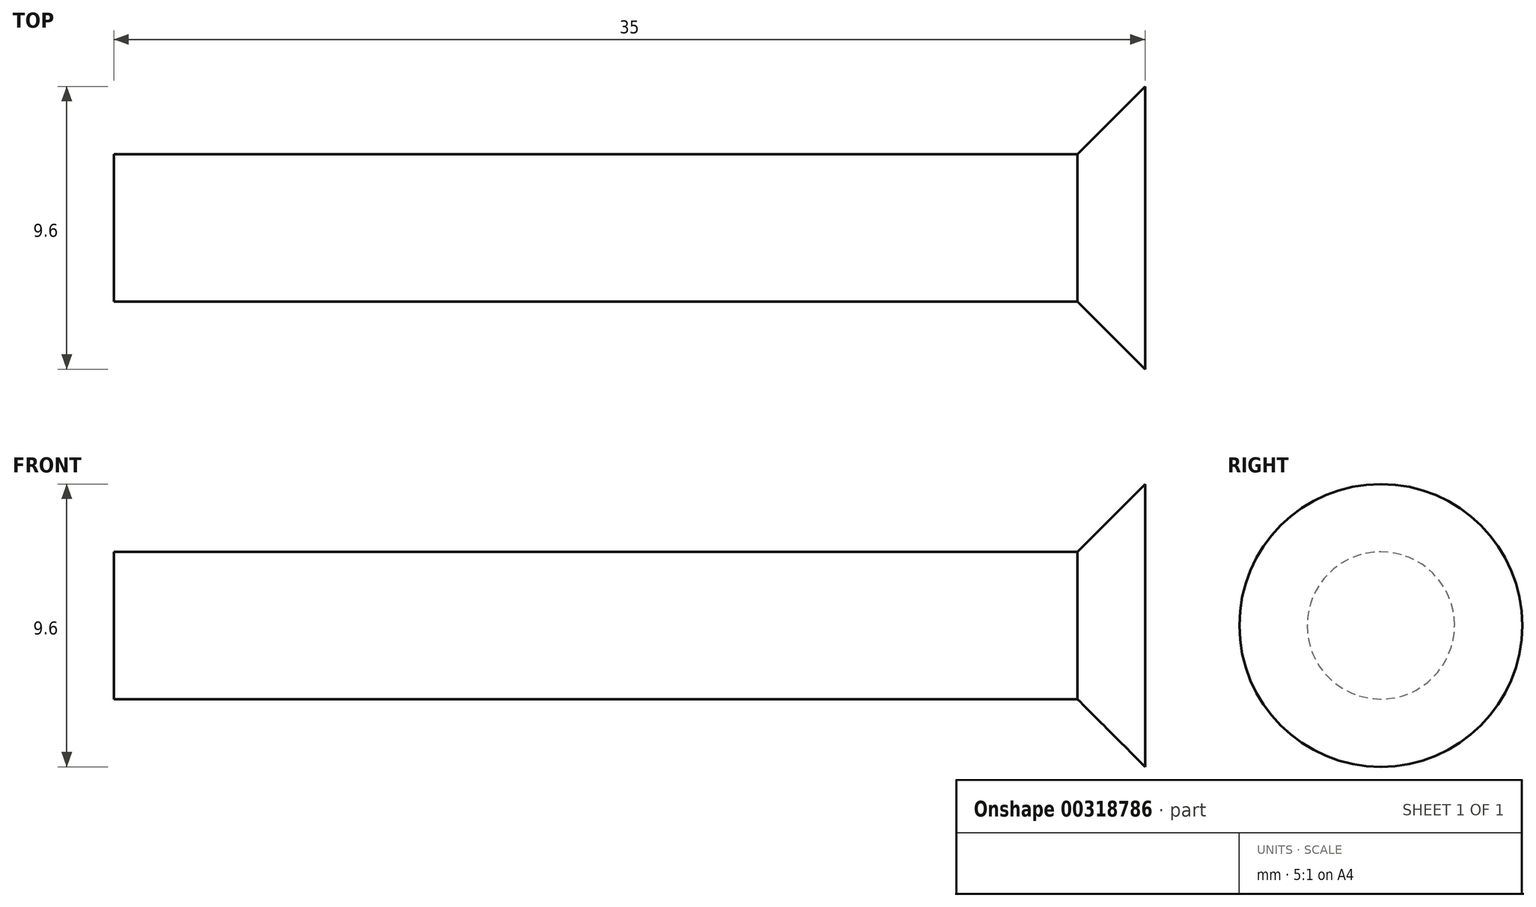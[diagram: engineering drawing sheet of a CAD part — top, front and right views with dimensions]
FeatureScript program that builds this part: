
annotation { "Feature Type Name" : "Feature", "Feature Type Description" : "" }
export const myFeature = defineFeature(function(context is Context, id is Id, definition is map)
    precondition{}
    {
        {
            var Q0;
            Q0=qCreatedBy(makeId("Right.planeOp"),FACE);
            var sketch = newSketch(context, id + "F0", { "sketchPlane" : qUnion([Q0])});
            skCircle(sketch, "E0", {"center": v(0, 0) * mm, "radius": 2.5 * mm});
            skSolve(sketch);
        }
        {
            var Q0;
            Q0=makeQuery(id+"F0.imprint","IMPRINT",FACE,{"disambiguationData":[TD([[makeQuery(id+"F0.imprint","IMPRINT",EDGE,{"derivedFrom":sQuery(id+"F0.wireOp",EDGE,"E0")}),1.0]])]});
            extrude(context, id + "F1", {"entities" : qUnion([Q0]), "depth" : 35 * mm});
        }
        {
            var Q0;
            Q0=makeQuery(id+"F1.opExtrude","CAP_FACE",FACE,{"disambiguationData":[OSD([sQuery(id+"F0.wireOp",EDGE,"E0")])],"isStart":false});
            var sketch = newSketch(context, id + "F2", { "sketchPlane" : qUnion([Q0])});
            skCircle(sketch, "E1", {"center": v(0, 0) * mm, "radius": 5 * mm});
            skSolve(sketch);
        }
        {
            var Q0;
            Q0=makeQuery(id+"F2.imprint","IMPRINT",FACE,{"disambiguationData":[TD([[makeQuery(id+"F2.imprint","IMPRINT",EDGE,{"derivedFrom":sQuery(id+"F2.wireOp",EDGE,"E1")}),1.0]])]});
            extrude(context, id + "F3", {"entities" : qUnion([Q0]), "operationType" : NewBodyOperationType.ADD, "oppositeDirection" : true, "depth" : 2.8 * mm});
        }
        {
            var Q0;
            Q0=makeQuery(id+"F3.opExtrude","CAP_EDGE",EDGE,{"disambiguationData":[OSD([sQuery(id+"F2.wireOp",EDGE,"E1")])],"isStart":false});
            chamfer(context, id + "F4", {"entities" : qUnion([Q0]), "width" : 3 * mm, "tangentPropagation" : true});
        }
    });
